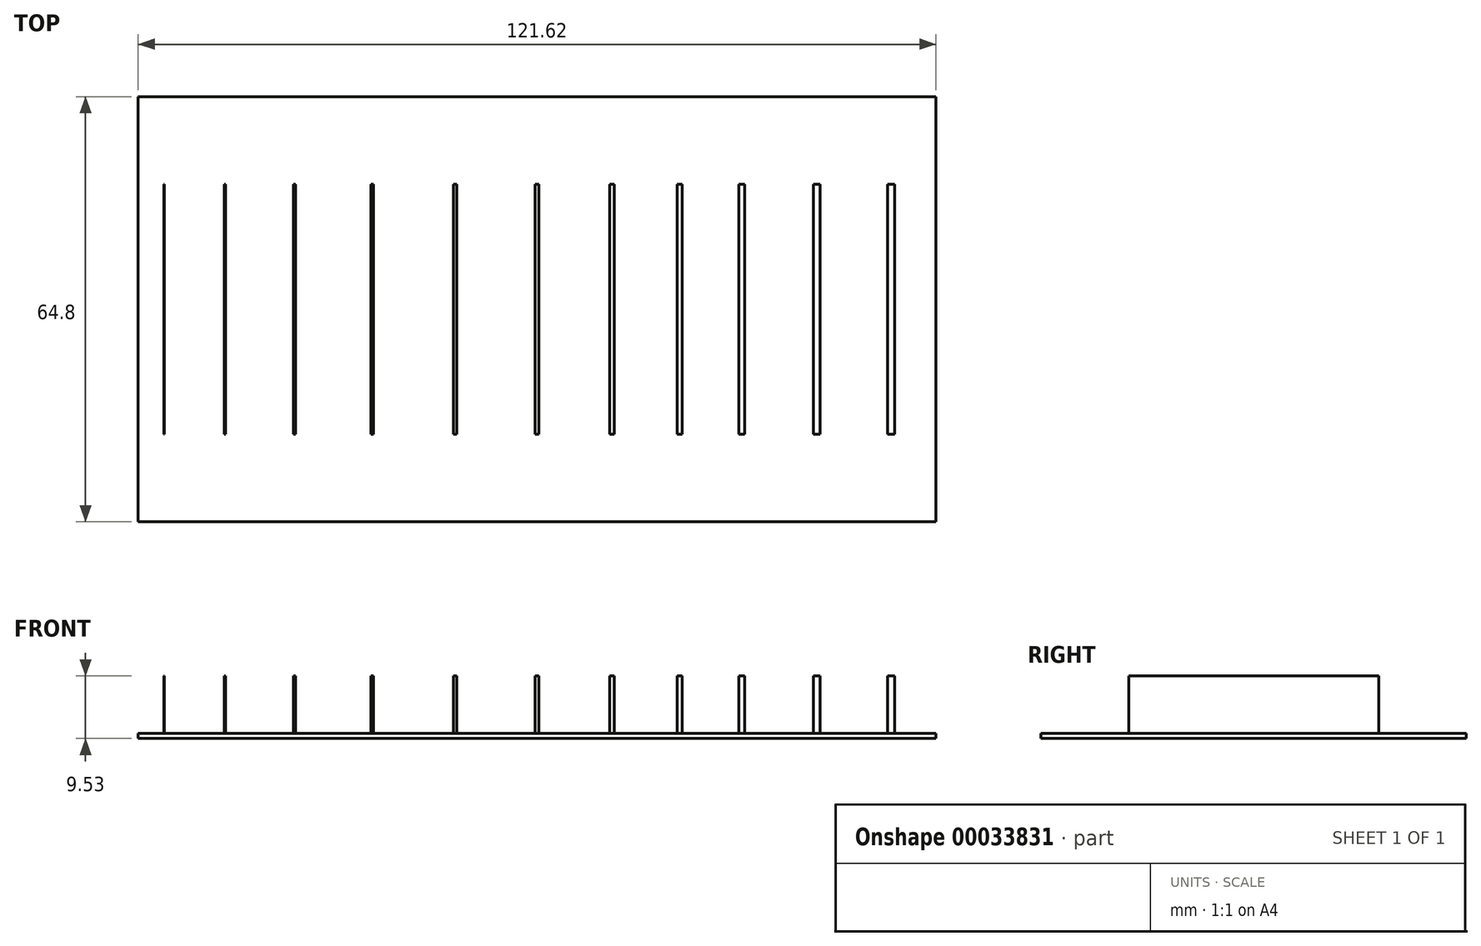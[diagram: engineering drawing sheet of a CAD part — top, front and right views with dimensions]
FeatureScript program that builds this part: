
annotation { "Feature Type Name" : "Feature", "Feature Type Description" : "" }
export const myFeature = defineFeature(function(context is Context, id is Id, definition is map)
    precondition{}
    {
        {
            var Q0;
            Q0=qCreatedBy(makeId("Top.planeOp"),FACE);
            var sketch = newSketch(context, id + "F0", { "sketchPlane" : qUnion([Q0])});
            skLineSegment(sketch, "E0.bottom", {"start": v(60.81, 32.4) * mm, "end": v(-60.81, 32.4) * mm});
            skLineSegment(sketch, "E0.top", {"start": v(60.81, -32.4) * mm, "end": v(-60.81, -32.4) * mm});
            skLineSegment(sketch, "E0.left", {"start": v(60.81, 32.4) * mm, "end": v(60.81, -32.4) * mm});
            skLineSegment(sketch, "E0.right", {"start": v(-60.81, 32.4) * mm, "end": v(-60.81, -32.4) * mm});
            skPoint(sketch, "E0.middle", {"position": v(0, 0) * mm});
            skSolve(sketch);
        }
        {
            var Q0;
            Q0 = qSketchRegion(id + "F0", true);
            extrude(context, id + "F1", {"entities" : qUnion([Q0]), "depth" : 0.8 * mm});
        }
        {
            var Q0;
            Q0=qCreatedBy(makeId("Top.planeOp"),FACE);
            var sketch = newSketch(context, id + "F2", { "sketchPlane" : qUnion([Q0])});
            skLineSegment(sketch, "E1", {"start": v(0, 56.57) * mm, "end": v(0, -52.97) * mm, "construction": true});
            skLineSegment(sketch, "E2", {"start": v(-12.47, 56.57) * mm, "end": v(-12.47, -52.97) * mm, "construction": true});
            skLineSegment(sketch, "E3", {"start": v(-25.12, -52.97) * mm, "end": v(-25.12, 56.57) * mm, "construction": true});
            skLineSegment(sketch, "E4", {"start": v(-36.96, 56.57) * mm, "end": v(-36.96, -52.97) * mm, "construction": true});
            skLineSegment(sketch, "E5", {"start": v(-47.6, -52.97) * mm, "end": v(-47.6, 56.57) * mm, "construction": true});
            skLineSegment(sketch, "E6", {"start": v(11.43, 56.57) * mm, "end": v(11.43, -52.97) * mm, "construction": true});
            skLineSegment(sketch, "E7", {"start": v(21.73, -52.97) * mm, "end": v(21.73, 56.57) * mm, "construction": true});
            skLineSegment(sketch, "E8", {"start": v(31.2, 56.57) * mm, "end": v(31.2, -52.97) * mm, "construction": true});
            skLineSegment(sketch, "E9", {"start": v(42.6, -52.97) * mm, "end": v(42.6, 56.57) * mm, "construction": true});
            skLineSegment(sketch, "E10", {"start": v(-56.86, 56.57) * mm, "end": v(-56.86, -52.97) * mm, "construction": true});
            skLineSegment(sketch, "E11", {"start": v(53.94, 56.57) * mm, "end": v(53.94, -52.97) * mm, "construction": true});
            skLineSegment(sketch, "E12.bottom", {"start": v(-56.9, 19.05) * mm, "end": v(-56.8, 19.05) * mm});
            skLineSegment(sketch, "E12.top", {"start": v(-56.9, -19.05) * mm, "end": v(-56.8, -19.05) * mm});
            skLineSegment(sketch, "E12.left", {"start": v(-56.9, 19.05) * mm, "end": v(-56.9, -19.05) * mm});
            skLineSegment(sketch, "E12.right", {"start": v(-56.8, 19.05) * mm, "end": v(-56.8, -19.05) * mm});
            skLineSegment(sketch, "E13.bottom", {"start": v(-47.7, 19.05) * mm, "end": v(-47.5, 19.05) * mm});
            skLineSegment(sketch, "E13.top", {"start": v(-47.7, -19.05) * mm, "end": v(-47.5, -19.05) * mm});
            skLineSegment(sketch, "E13.left", {"start": v(-47.7, 19.05) * mm, "end": v(-47.7, -19.05) * mm});
            skLineSegment(sketch, "E13.right", {"start": v(-47.5, 19.05) * mm, "end": v(-47.5, -19.05) * mm});
            skLineSegment(sketch, "E14.bottom", {"start": v(-37.1, 19.05) * mm, "end": v(-36.8, 19.05) * mm});
            skLineSegment(sketch, "E14.top", {"start": v(-37.1, -19.05) * mm, "end": v(-36.8, -19.05) * mm});
            skLineSegment(sketch, "E14.left", {"start": v(-37.1, 19.05) * mm, "end": v(-37.1, -19.05) * mm});
            skLineSegment(sketch, "E14.right", {"start": v(-36.8, 19.05) * mm, "end": v(-36.8, -19.05) * mm});
            skLineSegment(sketch, "E15.bottom", {"start": v(-25.32, 19.05) * mm, "end": v(-24.92, 19.05) * mm});
            skLineSegment(sketch, "E15.top", {"start": v(-25.32, -19.05) * mm, "end": v(-24.92, -19.05) * mm});
            skLineSegment(sketch, "E15.left", {"start": v(-25.32, 19.05) * mm, "end": v(-25.32, -19.05) * mm});
            skLineSegment(sketch, "E15.right", {"start": v(-24.92, 19.05) * mm, "end": v(-24.92, -19.05) * mm});
            skLineSegment(sketch, "E16.bottom", {"start": v(-12.72, 19.05) * mm, "end": v(-12.22, 19.05) * mm});
            skLineSegment(sketch, "E16.top", {"start": v(-12.72, -19.05) * mm, "end": v(-12.22, -19.05) * mm});
            skLineSegment(sketch, "E16.left", {"start": v(-12.72, 19.05) * mm, "end": v(-12.72, -19.05) * mm});
            skLineSegment(sketch, "E16.right", {"start": v(-12.22, 19.05) * mm, "end": v(-12.22, -19.05) * mm});
            skLineSegment(sketch, "E17.bottom", {"start": v(-0.3, 19.05) * mm, "end": v(0.3, 19.05) * mm});
            skLineSegment(sketch, "E17.top", {"start": v(-0.3, -19.05) * mm, "end": v(0.3, -19.05) * mm});
            skLineSegment(sketch, "E17.left", {"start": v(-0.3, 19.05) * mm, "end": v(-0.3, -19.05) * mm});
            skLineSegment(sketch, "E17.right", {"start": v(0.3, 19.05) * mm, "end": v(0.3, -19.05) * mm});
            skLineSegment(sketch, "E18.bottom", {"start": v(11.08, 19.05) * mm, "end": v(11.78, 19.05) * mm});
            skLineSegment(sketch, "E18.top", {"start": v(11.08, -19.05) * mm, "end": v(11.78, -19.05) * mm});
            skLineSegment(sketch, "E18.left", {"start": v(11.08, 19.05) * mm, "end": v(11.08, -19.05) * mm});
            skLineSegment(sketch, "E18.right", {"start": v(11.78, 19.05) * mm, "end": v(11.78, -19.05) * mm});
            skLineSegment(sketch, "E19.bottom", {"start": v(21.33, 19.05) * mm, "end": v(22.13, 19.05) * mm});
            skLineSegment(sketch, "E19.top", {"start": v(21.33, -19.05) * mm, "end": v(22.13, -19.05) * mm});
            skLineSegment(sketch, "E19.left", {"start": v(21.33, 19.05) * mm, "end": v(21.33, -19.05) * mm});
            skLineSegment(sketch, "E19.right", {"start": v(22.13, 19.05) * mm, "end": v(22.13, -19.05) * mm});
            skLineSegment(sketch, "E20.bottom", {"start": v(30.75, 19.05) * mm, "end": v(31.65, 19.05) * mm});
            skLineSegment(sketch, "E20.top", {"start": v(30.75, -19.05) * mm, "end": v(31.65, -19.05) * mm});
            skLineSegment(sketch, "E20.left", {"start": v(30.75, 19.05) * mm, "end": v(30.75, -19.05) * mm});
            skLineSegment(sketch, "E20.right", {"start": v(31.65, 19.05) * mm, "end": v(31.65, -19.05) * mm});
            skLineSegment(sketch, "E21.bottom", {"start": v(42.1, 19.05) * mm, "end": v(43.1, 19.05) * mm});
            skLineSegment(sketch, "E21.top", {"start": v(42.1, -19.05) * mm, "end": v(43.1, -19.05) * mm});
            skLineSegment(sketch, "E21.left", {"start": v(42.1, 19.05) * mm, "end": v(42.1, -19.05) * mm});
            skLineSegment(sketch, "E21.right", {"start": v(43.1, 19.05) * mm, "end": v(43.1, -19.05) * mm});
            skLineSegment(sketch, "E22.bottom", {"start": v(53.4, 19.05) * mm, "end": v(54.5, 19.05) * mm});
            skLineSegment(sketch, "E22.top", {"start": v(53.4, -19.05) * mm, "end": v(54.5, -19.05) * mm});
            skLineSegment(sketch, "E22.left", {"start": v(53.4, 19.05) * mm, "end": v(53.4, -19.05) * mm});
            skLineSegment(sketch, "E22.right", {"start": v(54.5, 19.05) * mm, "end": v(54.5, -19.05) * mm});
            skLineSegment(sketch, "E23", {"start": v(-64.67, 19.05) * mm, "end": v(68.6, 19.05) * mm, "construction": true});
            skLineSegment(sketch, "E24", {"start": v(-65.58, -19.05) * mm, "end": v(67.7, -19.05) * mm, "construction": true});
            skPoint(sketch, "E24.endSnap0", {"position": v(42.6, -19.05) * mm});
            skSolve(sketch);
        }
        {
            var Q0;
            Q0 = qSketchRegion(id + "F2", true);
            extrude(context, id + "F3", {"entities" : qUnion([Q0]), "operationType" : NewBodyOperationType.ADD, "depth" : 9.52 * mm});
        }
    });
